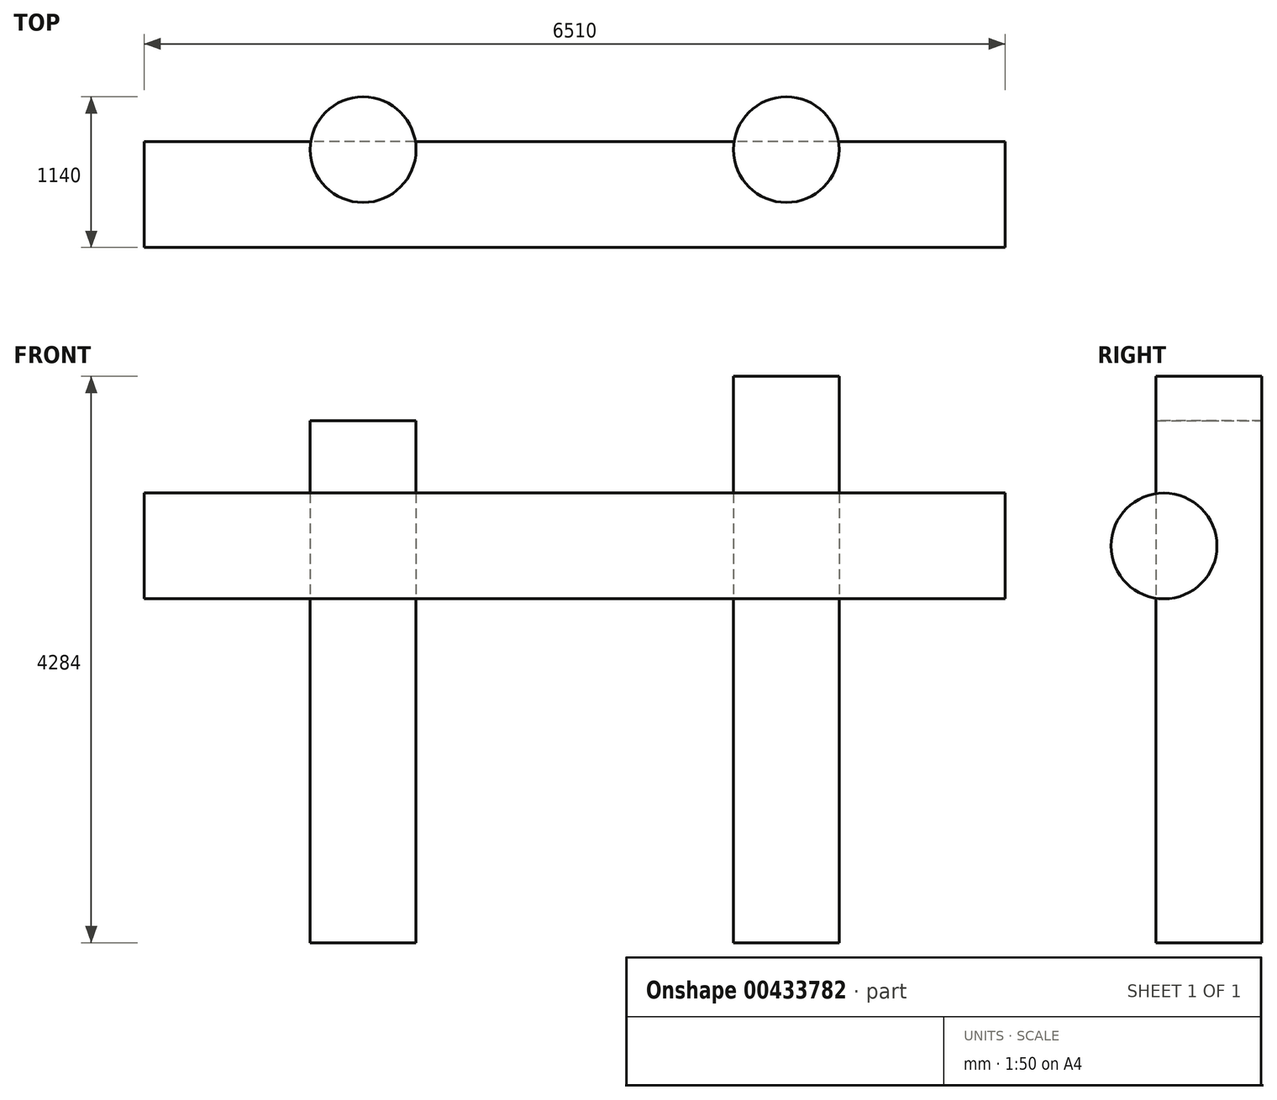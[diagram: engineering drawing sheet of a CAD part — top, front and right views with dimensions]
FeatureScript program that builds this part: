
annotation { "Feature Type Name" : "Feature", "Feature Type Description" : "" }
export const myFeature = defineFeature(function(context is Context, id is Id, definition is map)
    precondition{}
    {
        {
            var Q0;
            Q0=qCreatedBy(makeId("Right.planeOp"),FACE);
            var sketch = newSketch(context, id + "F0", { "sketchPlane" : qUnion([Q0])});
            skCircle(sketch, "E0", {"center": v(-340, 3001) * mm, "radius": 400 * mm});
            skSolve(sketch);
        }
        {
            var Q0;
            Q0 = qSketchRegion(id + "F0", true);
            extrude(context, id + "F1", {"entities" : qUnion([Q0]), "endBound" : BoundingType.SYMMETRIC, "depth" : 6510 * mm});
        }
        {
            var Q0;
            Q0=qCreatedBy(makeId("Top.planeOp"),FACE);
            var sketch = newSketch(context, id + "F2", { "sketchPlane" : qUnion([Q0])});
            skCircle(sketch, "E1", {"center": v(-1600, 0) * mm, "radius": 400 * mm});
            skSolve(sketch);
        }
        {
            var Q0;
            Q0 = qSketchRegion(id + "F2", true);
            extrude(context, id + "F3", {"entities" : qUnion([Q0]), "depth" : 3950 * mm});
        }
        {
            var Q0;
            Q0=qCreatedBy(makeId("Top.planeOp"),FACE);
            var sketch = newSketch(context, id + "F4", { "sketchPlane" : qUnion([Q0])});
            skCircle(sketch, "E2", {"center": v(1600, 0) * mm, "radius": 400 * mm});
            skSolve(sketch);
        }
        {
            var Q0;
            Q0 = qSketchRegion(id + "F4", true);
            extrude(context, id + "F5", {"entities" : qUnion([Q0]), "depth" : 4284 * mm});
        }
    });
